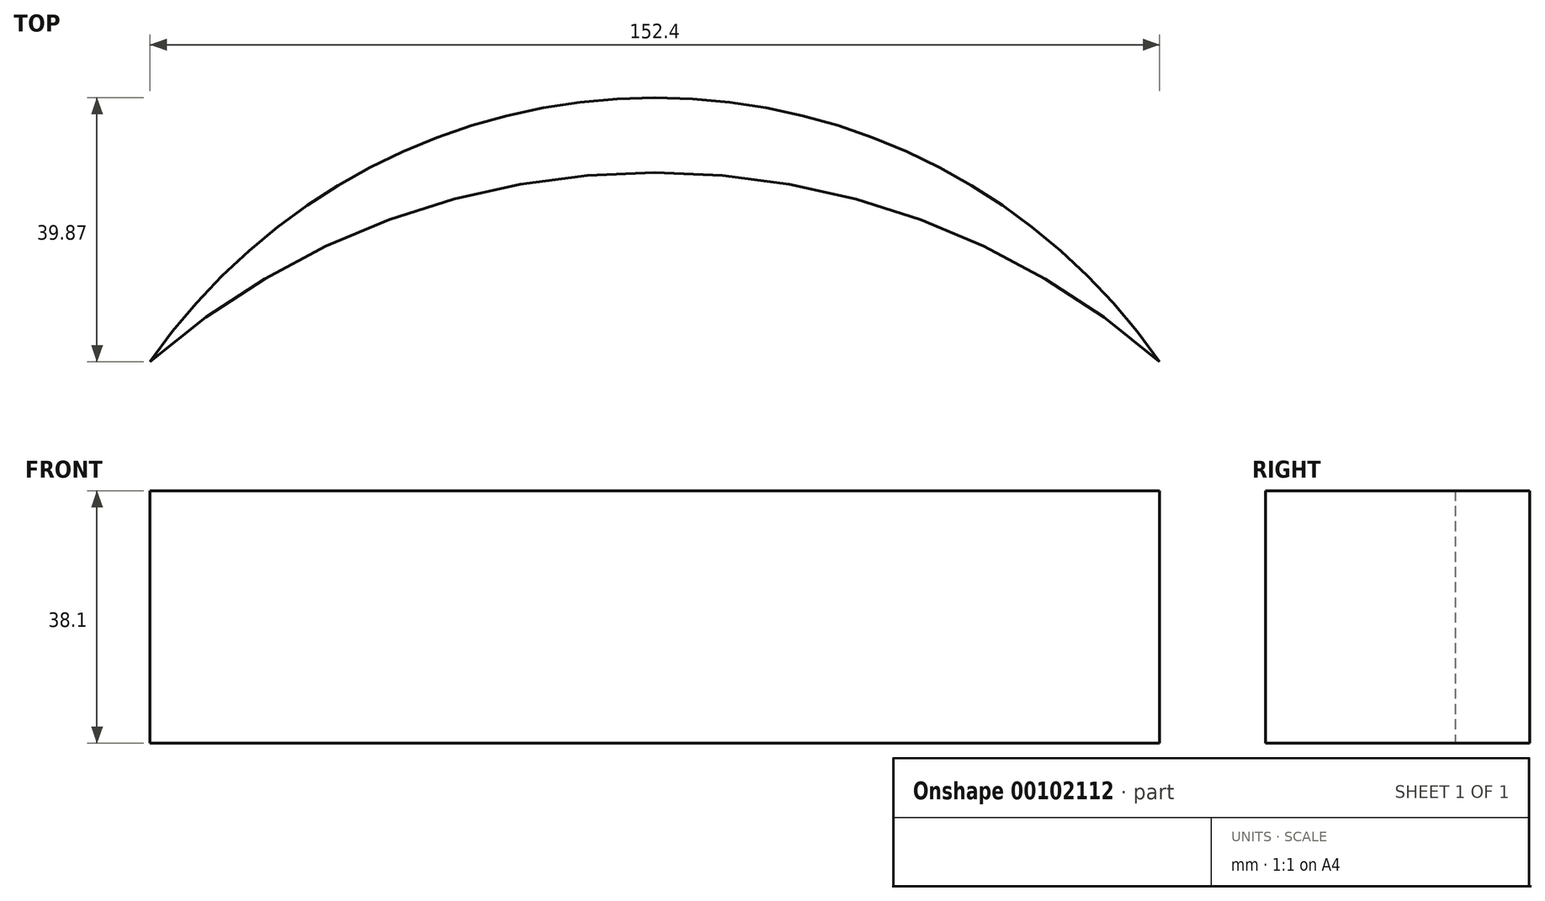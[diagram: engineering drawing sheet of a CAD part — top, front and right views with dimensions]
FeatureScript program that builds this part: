
annotation { "Feature Type Name" : "Feature", "Feature Type Description" : "" }
export const myFeature = defineFeature(function(context is Context, id is Id, definition is map)
    precondition{}
    {
        {
            var Q0;
            Q0=qCreatedBy(makeId("Top.planeOp"),FACE);
            var sketch = newSketch(context, id + "F0", { "sketchPlane" : qUnion([Q0])});
            skArc(sketch, "E0", {"start": v(75.9, 0) * mm, "mid": v(-0.3, 39.87) * mm, "end": v(-76.5, 0) * mm});
            skArc(sketch, "E1", {"start": v(75.9, 0) * mm, "mid": v(-0.3, 28.6) * mm, "end": v(-76.5, 0) * mm});
            skSolve(sketch);
        }
        {
            var Q0;
            Q0 = qSketchRegion(id + "F0", true);
            extrude(context, id + "F1", {"entities" : qUnion([Q0]), "depth" : 38.1 * mm});
        }
    });
